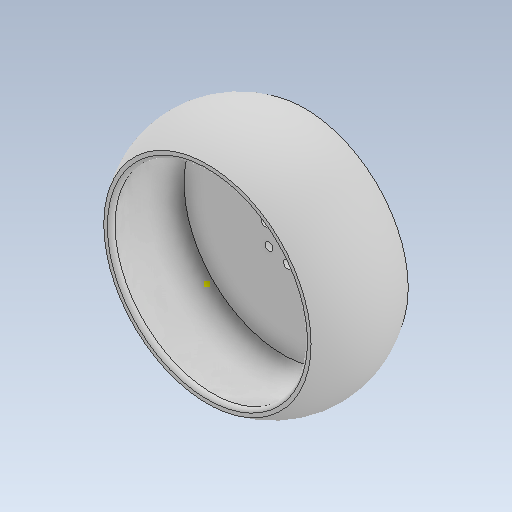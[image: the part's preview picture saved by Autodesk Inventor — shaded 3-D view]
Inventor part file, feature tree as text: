
AUTODESK INVENTOR PART (.ipt)
format: ipt  version: 2020 (Build 240168000, 168)  size: 444,416 bytes
history: native  units: mm
features: sketch x6, other x4, extrude x3, reference x2, sweep x1, shell x1, fillet x1, projected_geometry x1
ambient origin geometry x8: Origin, YZ Plane, XZ Plane, XY Plane, X Axis, Y Axis, Z Axis, Center Point
bodies: Solid1 (feature_tree)
feature tree (19):
  sweep  "Sweep1"
  shell  "Shell1"  Thickness=12.0mm
  extrude  "Extrusion1"  Depth=15.0mm
  extrude  "Extrusion2"  Depth=2.5mm
  extrude  "Extrusion3"  Depth=10.0mm
  fillet  "Fillet1"  Radius=10.0mm
  sketch  "Sketch8"  dims[d15=1.0mm]
  sketch  "Sketch1"  dims[d0=75.0mm d1=50.0mm d2=12.0mm]
  sketch  "Sketch2"  dims[d3=30.0mm d4=15.0mm]
  sketch  "Sketch4"  dims[d5=0.0mm d6=0.0mm d7=2.5mm]
  reference  "Reference1"
  reference  "Reference2"
  sketch  "Sketch6"  dims[d8=10.0mm d9=0.0mm d10=5.0mm d11=10.0mm d12=0.0mm]
  sketch  "Sketch7"  dims[d13=4.0mm d14=0.0mm]
  projected_geometry  "Projected Loop1"
  other  "<userpath>\Desktop\KangKangBalancing\KangKang.iam"
  other  "KangKang.iam"
  other  "tarot_5008_340kv_assy:1"
  other  "housing0:1"
